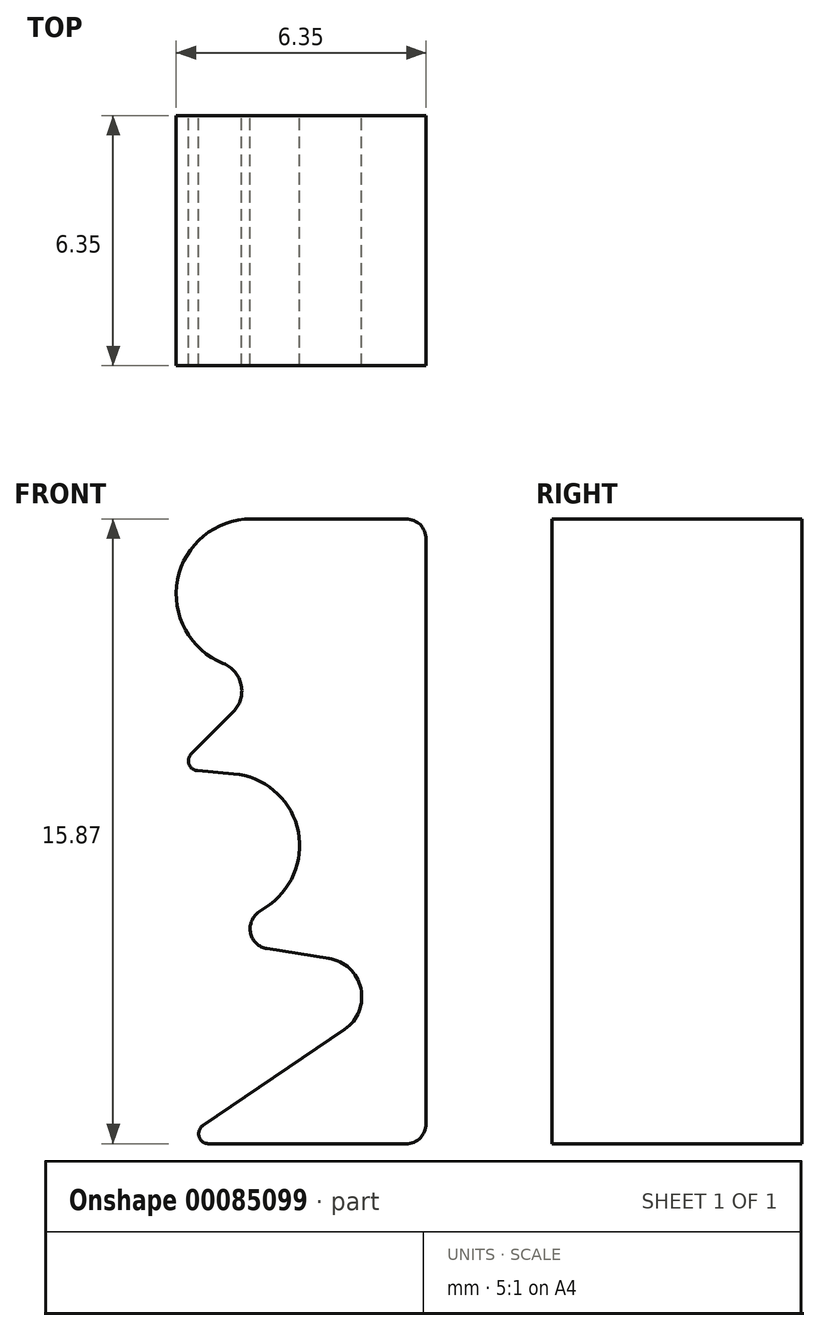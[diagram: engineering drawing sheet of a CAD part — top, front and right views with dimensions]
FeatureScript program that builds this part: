
annotation { "Feature Type Name" : "Feature", "Feature Type Description" : "" }
export const myFeature = defineFeature(function(context is Context, id is Id, definition is map)
    precondition{}
    {
        {
            var Q0;
            Q0=qCreatedBy(makeId("Front.planeOp"),FACE);
            var sketch = newSketch(context, id + "F0", { "sketchPlane" : qUnion([Q0])});
            skLineSegment(sketch, "E0", {"start": v(6.35, 4.4) * mm, "end": v(6.35, -6.65) * mm});
            skLineSegment(sketch, "E1", {"start": v(5.84, 4.9) * mm, "end": v(1.9, 4.9) * mm});
            skLineSegment(sketch, "E2", {"start": v(6.35, -6.65) * mm, "end": v(6.35, -10.46) * mm});
            skArc(sketch, "E3", {"start": v(0.83, -10.97) * mm, "mid": v(0.58, -10.8) * mm, "end": v(0.68, -10.5) * mm});
            skLineSegment(sketch, "E4", {"start": v(0.68, -10.5) * mm, "end": v(4.94, -7.62) * mm});
            skArc(sketch, "E5", {"start": v(6.35, -10.46) * mm, "mid": v(6.2, -10.82) * mm, "end": v(5.84, -10.97) * mm});
            skLineSegment(sketch, "E6", {"start": v(0.83, -10.97) * mm, "end": v(5.84, -10.97) * mm});
            skLineSegment(sketch, "E7", {"start": v(0, 4.9) * mm, "end": v(6.2, -10.82) * mm, "construction": true});
            skArc(sketch, "E8", {"start": v(1.9, 4.9) * mm, "mid": v(0.03, 3.36) * mm, "end": v(1.2, 1.23) * mm});
            skLineSegment(sketch, "E9", {"start": v(0, 4.9) * mm, "end": v(0, -10.97) * mm, "construction": true});
            skLineSegment(sketch, "E10", {"start": v(0.83, -10.97) * mm, "end": v(0, -10.97) * mm, "construction": true});
            skArc(sketch, "E11", {"start": v(5.84, 4.9) * mm, "mid": v(6.2, 4.75) * mm, "end": v(6.35, 4.4) * mm});
            skLineSegment(sketch, "E12", {"start": v(5.84, 4.9) * mm, "end": v(6.35, 4.9) * mm, "construction": true});
            skLineSegment(sketch, "E13", {"start": v(6.35, 4.9) * mm, "end": v(6.35, 4.4) * mm, "construction": true});
            skLineSegment(sketch, "E14", {"start": v(5.84, -10.97) * mm, "end": v(6.35, -10.97) * mm, "construction": true});
            skLineSegment(sketch, "E15", {"start": v(6.35, -10.97) * mm, "end": v(6.35, -10.46) * mm, "construction": true});
            skLineSegment(sketch, "E16", {"start": v(0, -10.97) * mm, "end": v(6.35, -6.65) * mm, "construction": true});
            skLineSegment(sketch, "E17", {"start": v(6.35, 4.9) * mm, "end": v(0, -1.45) * mm, "construction": true});
            skLineSegment(sketch, "E18", {"start": v(6.35, -6.65) * mm, "end": v(0, -5.65) * mm, "construction": true});
            skArc(sketch, "E19", {"start": v(4.28, -8.06) * mm, "mid": v(4.7, -7.02) * mm, "end": v(3.88, -6.26) * mm});
            skLineSegment(sketch, "E20", {"start": v(0, -6.62) * mm, "end": v(6.35, -2) * mm, "construction": true});
            skArc(sketch, "E21", {"start": v(2.09, -5.1) * mm, "mid": v(1.9, -5.63) * mm, "end": v(2.3, -6.01) * mm});
            skLineSegment(sketch, "E22", {"start": v(2.3, -6.01) * mm, "end": v(3.88, -6.26) * mm});
            skLineSegment(sketch, "E23", {"start": v(0, -1.45) * mm, "end": v(6.35, -2) * mm, "construction": true});
            skArc(sketch, "E24", {"start": v(2.38, -4.89) * mm, "mid": v(3.07, -2.91) * mm, "end": v(1.46, -1.57) * mm});
            skArc(sketch, "E25", {"start": v(0.39, -1.06) * mm, "mid": v(0.33, -1.33) * mm, "end": v(0.54, -1.5) * mm});
            skLineSegment(sketch, "E26", {"start": v(0.54, -1.5) * mm, "end": v(1.46, -1.57) * mm});
            skLineSegment(sketch, "E27", {"start": v(0.39, -1.06) * mm, "end": v(1.45, 0) * mm});
            skLineSegment(sketch, "E28", {"start": v(2.09, -5.1) * mm, "end": v(2.38, -4.89) * mm});
            skArc(sketch, "E29", {"start": v(1.45, 0) * mm, "mid": v(1.65, 0.68) * mm, "end": v(1.2, 1.23) * mm});
            skSolve(sketch);
        }
        {
            var Q0;
            Q0=makeQuery(id+"F0.imprint","IMPRINT",FACE,{"disambiguationData":[TD([[makeQuery(id+"F0.imprint","IMPRINT",EDGE,{"derivedFrom":sQuery(id+"F0.wireOp",EDGE,"E0")}),-1.0]])]});
            extrude(context, id + "F1", {"entities" : qUnion([Q0]), "depth" : 6.35 * mm});
        }
    });
